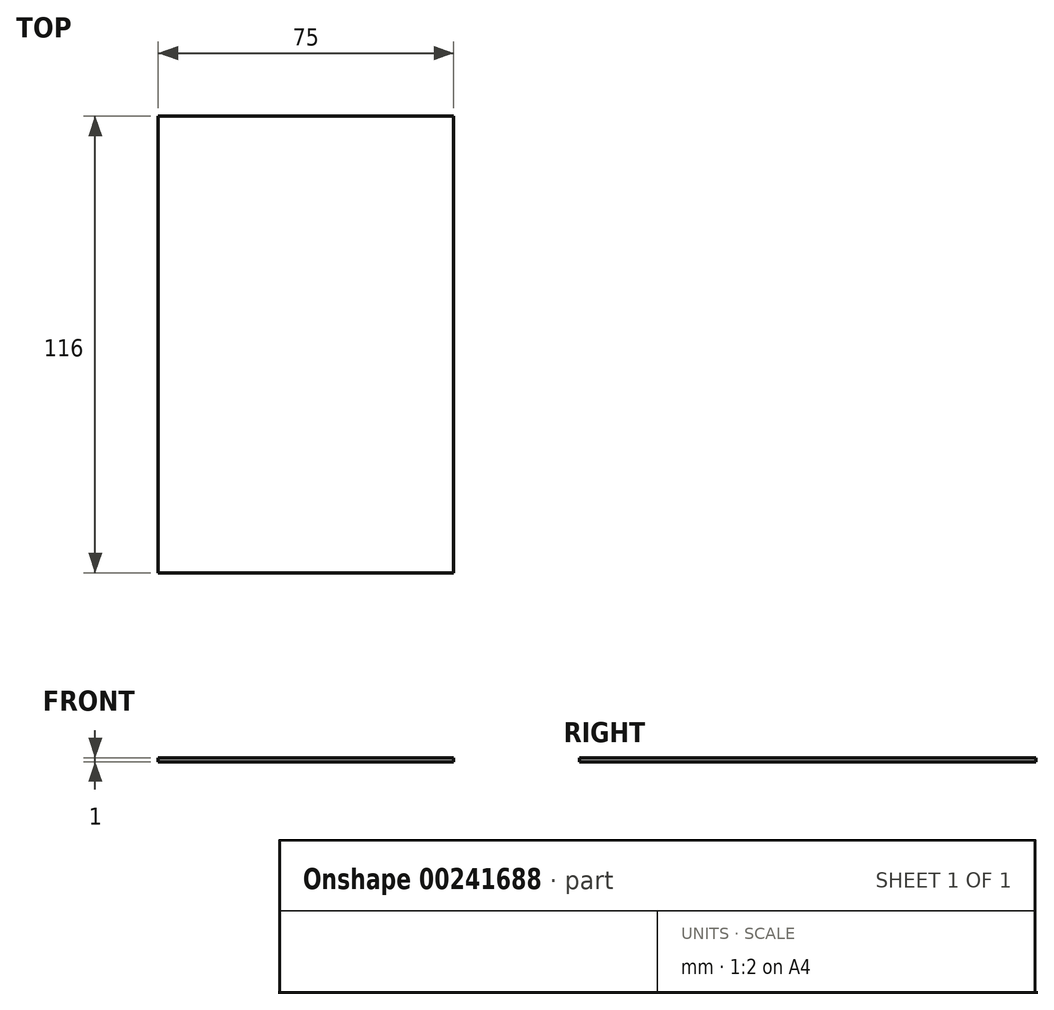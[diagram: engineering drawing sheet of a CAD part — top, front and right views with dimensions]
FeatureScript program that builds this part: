
annotation { "Feature Type Name" : "Feature", "Feature Type Description" : "" }
export const myFeature = defineFeature(function(context is Context, id is Id, definition is map)
    precondition{}
    {
        {
            var Q0;
            Q0=qCreatedBy(makeId("Top.planeOp"),FACE);
            var sketch = newSketch(context, id + "F0", { "sketchPlane" : qUnion([Q0])});
            skLineSegment(sketch, "E0.bottom", {"start": v(37.5, -58) * mm, "end": v(-37.5, -58) * mm});
            skLineSegment(sketch, "E0.top", {"start": v(37.5, 58) * mm, "end": v(-37.5, 58) * mm});
            skLineSegment(sketch, "E0.left", {"start": v(37.5, -58) * mm, "end": v(37.5, 58) * mm});
            skLineSegment(sketch, "E0.right", {"start": v(-37.5, -58) * mm, "end": v(-37.5, 58) * mm});
            skPoint(sketch, "E0.middle", {"position": v(0, 0) * mm});
            skSolve(sketch);
        }
        {
            var Q0;
            Q0=makeQuery(id+"F0.imprint","IMPRINT",FACE,{"disambiguationData":[TD([[makeQuery(id+"F0.imprint","IMPRINT",EDGE,{"derivedFrom":sQuery(id+"F0.wireOp",EDGE,"E0.bottom")}),-1.0]])]});
            extrude(context, id + "F1", {"entities" : qUnion([Q0]), "depth" : 1 * mm});
        }
    });
